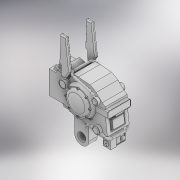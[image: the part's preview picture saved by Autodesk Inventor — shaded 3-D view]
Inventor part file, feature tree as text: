
AUTODESK INVENTOR PART (.ipt)
format: ipt  version: 2022 (Build 260153000, 153)  size: 1,223,680 bytes
history: native  units: mm
features: sketch x39, extrude x35, fillet x6, plane x5, projected_geometry x5, chamfer x4, sweep x3, revolve x2, pattern_circular x2, mirror x2
ambient origin geometry x8: Origin, YZ Plane, XZ Plane, XY Plane, X Axis, Y Axis, Z Axis, Center Point
bodies: Solid1 (feature_tree)
feature tree (103):
  extrude  "Extrusion1"  Depth=3.5mm
  extrude  "Extrusion2"  Depth=3.0mm
  extrude  "Extrusion3"  Depth=4.5mm
  extrude  "Extrusion4"  Depth=2.0mm
  extrude  "Extrusion5"  Depth=1.0mm
  chamfer  "Chamfer1"  Distance=10.5mm
  extrude  "Extrusion6"  Depth=0.75mm TaperAngle=0.0deg
  extrude  "Extrusion7"  Depth=7.0mm
  extrude  "Extrusion8"  Depth=0.75mm
  fillet  "Fillet1"  Radius=0.75mm
  revolve  "Revolution1"  [1 undecoded]
  sketch  "Sketch10"  dims[d14=14.5mm]
  extrude  "Extrusion12"  Depth=0.75mm
  extrude  "Extrusion9"  Depth=0.75mm
  extrude  "Extrusion10"  Depth=0.75mm
  pattern_circular  "Circular Pattern1"  [2 undecoded]
  extrude  "Extrusion11"  Depth=0.75mm TaperAngle=0.0deg
  fillet  "Fillet2"  Radius=11.0mm
  fillet  "Fillet3"  Radius=3.5mm
  extrude  "Extrusion13"  Depth=0.5mm
  extrude  "Extrusion14"  Depth=0.5mm
  extrude  "Extrusion15"  Depth=0.5mm
  pattern_circular  "Circular Pattern2"  [2 undecoded]
  sketch  "Sketch18"  dims[d20=3.348045mm]
  extrude  "Extrusion16"  Depth=0.75mm TaperAngle=0.0deg
  extrude  "Extrusion17"  Depth=0.75mm TaperAngle=0.0deg
  extrude  "Extrusion18"  Depth=0.5mm TaperAngle=45.0deg
  extrude  "Extrusion19"  Depth=0.75mm
  extrude  "Extrusion20"  Depth=0.75mm
  extrude  "Extrusion21"  Depth=0.75mm TaperAngle=0.0deg
  extrude  "Extrusion22"  Depth=0.75mm
  extrude  "Extrusion23"  Depth=0.75mm
  plane  "Work Plane1"
  revolve  "Revolution2"  [1 undecoded]
  extrude  "Extrusion24"  Depth=0.75mm
  extrude  "Extrusion25"  Depth=10.0mm TaperAngle=0.0deg
  extrude  "Extrusion26"  Depth=0.5mm
  extrude  "Extrusion27"  Depth=0.75mm
  extrude  "Extrusion28"  Depth=0.75mm
  plane  "Work Plane2"
  sketch  "Sketch29"  dims[d32=9.0mm]
  extrude  "Extrusion29"  Depth=0.75mm
  fillet  "Fillet4"  Radius=2.0mm
  chamfer  "Chamfer2"  Distance=2.0mm
  fillet  "Fillet5"  Radius=1.0mm
  plane  "Work Plane3"
  sweep  "Sweep1"
  sketch  "Sketch32"  dims[d34=10.0mm]
  extrude  "Extrusion30"  Depth=0.5mm
  extrude  "Extrusion31"  TaperAngle=90.0deg  [1 undecoded]
  sketch  "Sketch33"  dims[d35=9.5mm]
  chamfer  "Chamfer3"  Distance=15.0mm
  chamfer  "Chamfer4"  Distance=0.4mm
  mirror  "Mirror1"
  plane  "Work Plane4"
  sketch  "Sketch34"  dims[d36=5.0mm]
  sweep  "Sweep3"
  sweep  "Sweep4"
  mirror  "Mirror2"
  sketch  "Sketch37"  dims[d39=8.0mm]
  extrude  "Extrusion32"  Depth=0.75mm TaperAngle=0.0deg
  plane  "Work Plane5"
  extrude  "Extrusion33"  Depth=0.75mm TaperAngle=360.0deg
  fillet  "Fillet6"  Radius=0.9mm
  extrude  "Extrusion34"  Depth=0.5mm
  extrude  "Extrusion35"  Depth=0.5mm
  sketch  "Sketch1"  dims[d0=12.0mm d1=3.5mm]
  sketch  "Sketch2"  dims[d2=12.0mm d3=3.0mm]
  sketch  "Sketch3"  dims[d4=1.0mm d5=4.5mm]
  sketch  "Sketch4"  dims[d6=3.0mm d7=2.0mm]
  sketch  "Sketch5"  dims[d8=1.0mm d9=1.0mm]
  projected_geometry  "Projected Loop1"
  sketch  "Sketch6"  dims[d10=1.5mm]
  sketch  "Sketch7"  dims[d11=7.0mm]
  sketch  "Sketch8"  dims[d12=10.0mm]
  sketch  "Sketch9"  dims[d13=13.0mm]
  sketch  "Sketch11"  dims[d15=14.5mm]
  sketch  "Sketch12"  dims[d16=15.5mm]
  sketch  "Sketch15"  dims[d17=10.5mm]
  sketch  "Sketch16"  dims[d18=11.0mm]
  sketch  "Sketch17"  dims[d19=5.5mm]
  projected_geometry  "Projected Loop3"
  sketch  "Sketch19"  dims[d21=13.0mm]
  projected_geometry  "Projected Loop4"
  sketch  "Sketch20"  dims[d23=3.0mm]
  projected_geometry  "Projected Loop5"
  sketch  "Sketch21"  dims[d24=7.0mm]
  sketch  "Sketch22"  dims[d25=2.0mm]
  sketch  "Sketch23"  dims[d26=7.5mm]
  sketch  "Sketch24"  dims[d27=7.0mm]
  sketch  "Sketch25"  dims[d28=6.0mm]
  sketch  "Sketch26"  dims[d29=6.0mm]
  sketch  "Sketch27"  dims[d30=6.0mm]
  sketch  "Sketch28"  dims[d31=8.5mm]
  sketch  "Sketch31"  dims[d33=10.0mm]
  sketch  "3D Sketch1"
  sketch  "Sketch35"  dims[d37=4.0mm]
  sketch  "3D Sketch6"
  sketch  "Sketch36"  dims[d38=0.0mm]
  sketch  "Sketch38"  dims[d40=10.0mm]
  sketch  "Sketch39"  dims[d41=10.5mm]
  projected_geometry  "Projected Loop6"
  sketch  "Sketch40"  dims[d42=10.0mm d43=10.5mm d44=10.5mm d45=0.0mm d47=7.0mm d48=5.5mm d49=0.75mm d50=0.75mm d51=0.75mm d52=0.75mm d53=1.0mm d54=3.0mm d55=0.0mm d56=3.5mm d57=0.0mm d58=11.0mm d59=3.5mm d60=0.5mm d61=0.5mm d62=0.5mm d65=0.5mm d66=1.5mm d67=5.0mm d68=0.0mm d69=0.0mm d70=0.25mm d71=0.0mm d72=0.5mm d73=2.0mm d74=45.0deg d75=0.25mm d76=0.2mm d77=0.25mm d78=0.0mm d79=5.0mm d80=2.5mm d81=2.0mm d82=0.0mm d83=1.0mm d84=10.0mm d85=0.0mm d86=0.5mm d87=12.0mm d88=14.0mm d89=1.5mm d90=2.0mm d91=2.0mm d93=1.0mm d94=1.5mm d95=0.5mm d96=90.0deg d97=15.0mm d98=0.4mm d99=0.425mm d100=1.0mm d101=0.0mm d102=0.6mm d103=0.0mm d104=80.0mm d105=360.0deg d107=0.9mm d108=0.0mm d109=0.5mm d110=0.5mm d111=0.9mm d112=0.0mm d113=1.3mm d114=2.15mm d115=0.0mm d116=0.5mm d117=1.0mm d118=0.5mm d119=0.0mm d120=0.6mm d121=0.0mm d122=20.0mm d123=1551.248639mm d125=4.5mm d126=0.75mm d127=3.5mm d128=1.5mm d129=0.25mm d130=3.0mm d131=2.5mm d132=0.25mm d133=0.75mm d134=0.75mm d135=3.0mm d136=8.0mm d137=0.0mm d138=7.5mm d139=0.0mm d140=6.75mm d141=0.0mm d142=0.3mm d143=0.25mm d144=0.25mm d145=0.0mm d146=3.25mm d147=3.75mm d148=1.0mm d149=0.2mm d150=0.5mm d151=2.5mm d152=7.5mm d153=0.0mm d154=0.25mm d155=0.0mm d156=0.25mm d157=0.0mm d158=0.25mm d159=0.0mm d160=90.0deg d161=2.5mm d162=0.25mm d163=0.0mm d164=0.1mm d165=0.0mm d166=0.1mm d167=0.0mm d168=3.5mm d169=2.1mm d170=0.0mm d171=0.1mm d172=0.0mm d173=1.5mm d174=0.0mm d175=0.5mm d176=0.5mm d177=2.0mm d178=45.0deg d179=0.5mm d180=1.0mm d181=0.0mm d182=0.0mm d183=3.5mm d184=3.0mm d187=1.3mm d188=0.0mm d189=1.6mm d190=0.0mm d191=0.25mm d192=2.0mm d193=45.0deg d194=0.25mm d195=2.0mm d196=45.0deg d197=2.0mm d198=2.0mm d199=1.0mm d202=0.0mm d203=0.0mm d204=2.0mm d205=2.0mm d206=2.0mm d207=1.0mm d208=0.0mm d209=0.0mm d210=4.0mm d211=7.0mm d212=8.0mm d213=4.0mm d214=0.0mm d217=1.679781mm d218=13.912215mm d219=3.472939mm d220=2.026421mm d221=2.206562mm d222=0.047706mm d223=0.098811mm d224=0.875272mm d225=16.767391mm d226=20.497253mm d227=21.206034mm d228=90.0deg d229=9.0mm d230=10.5mm d231=0.0mm d232=6.0mm d233=10.5mm d234=0.0mm d235=0.75mm d236=0.0mm]
note: 7 required parameter values undecoded (feature->parameter linkage not recoverable at this tier; creation-order binding heuristic only, values carry confidence <= 0.55)